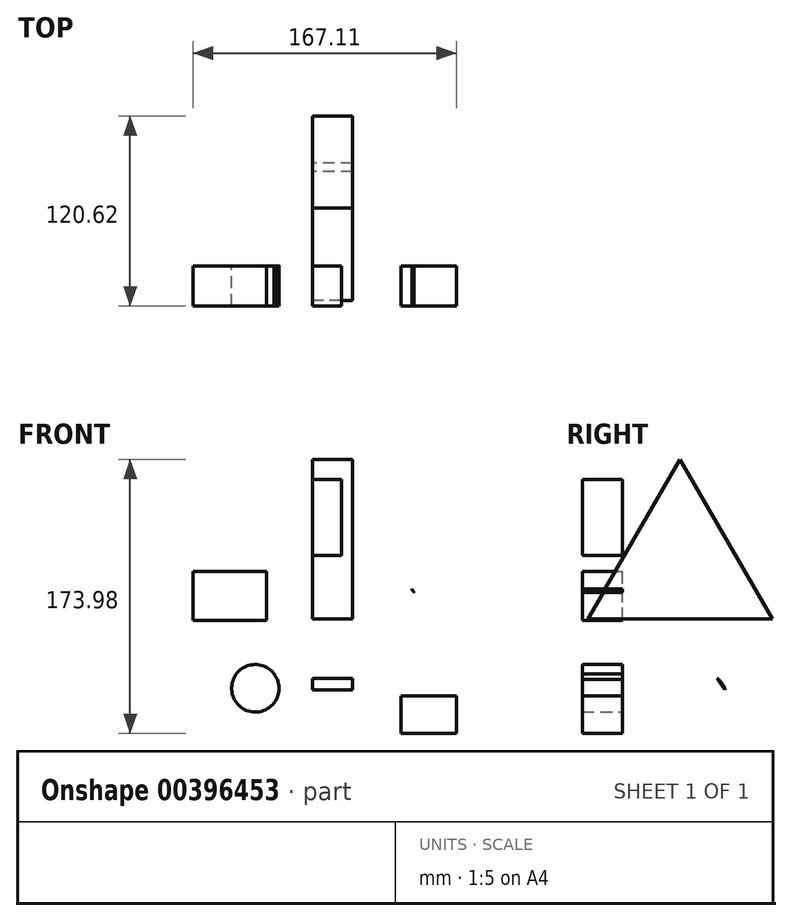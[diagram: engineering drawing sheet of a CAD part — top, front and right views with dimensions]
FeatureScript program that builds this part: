
annotation { "Feature Type Name" : "Feature", "Feature Type Description" : "" }
export const myFeature = defineFeature(function(context is Context, id is Id, definition is map)
    precondition{}
    {
        {
            var Q0;
            Q0=qCreatedBy(makeId("Front.planeOp"),FACE);
            var sketch = newSketch(context, id + "F0", { "sketchPlane" : qUnion([Q0])});
            skCircle(sketch, "E0", {"center": v(21.2, 12.78) * mm, "radius": 51.47 * mm});
            skPoint(sketch, "E0.first.point", {"position": v(62.94, 42.9) * mm});
            skPoint(sketch, "E0.second.point", {"position": v(-22.4, -14.6) * mm});
            skPoint(sketch, "E0.third.point", {"position": v(-28.66, 0) * mm});
            skCircle(sketch, "E1", {"center": v(70.23, 46.45) * mm, "radius": 8.11 * mm});
            skPoint(sketch, "E1.second.point", {"position": v(75.6, 52.52) * mm});
            skPoint(sketch, "E1.third.point", {"position": v(77.52, 42.9) * mm});
            skCircle(sketch, "E2", {"center": v(-36.43, -20.12) * mm, "radius": 15.08 * mm});
            skPoint(sketch, "E2.second.point", {"position": v(-48.03, -29.76) * mm});
            skPoint(sketch, "E2.third.point", {"position": v(-36.88, -5.04) * mm});
            skLineSegment(sketch, "E3.bottom", {"start": v(-29.25, 23.04) * mm, "end": v(-75.87, 23.04) * mm});
            skLineSegment(sketch, "E3.top", {"start": v(-29.25, 54.17) * mm, "end": v(-75.87, 54.17) * mm});
            skLineSegment(sketch, "E3.left", {"start": v(-29.25, 23.04) * mm, "end": v(-29.25, 54.17) * mm});
            skLineSegment(sketch, "E3.right", {"start": v(-75.87, 23.04) * mm, "end": v(-75.87, 54.17) * mm});
            skLineSegment(sketch, "E4.bottom", {"start": v(56.14, -25) * mm, "end": v(91.24, -25) * mm});
            skLineSegment(sketch, "E4.top", {"start": v(56.14, -48.76) * mm, "end": v(91.24, -48.76) * mm});
            skLineSegment(sketch, "E4.left", {"start": v(56.14, -25) * mm, "end": v(56.14, -48.76) * mm});
            skLineSegment(sketch, "E4.right", {"start": v(91.24, -25) * mm, "end": v(91.24, -48.76) * mm});
            skLineSegment(sketch, "E5.bottom", {"start": v(18.33, 64.17) * mm, "end": v(0, 64.17) * mm});
            skLineSegment(sketch, "E5.top", {"start": v(18.33, 112.4) * mm, "end": v(0, 112.4) * mm});
            skLineSegment(sketch, "E5.left", {"start": v(18.33, 64.17) * mm, "end": v(18.33, 112.4) * mm});
            skLineSegment(sketch, "E5.right", {"start": v(0, 64.17) * mm, "end": v(0, 112.4) * mm});
            skLineSegment(sketch, "E6", {"start": v(91.24, -48.76) * mm, "end": v(137.36, -96.51) * mm});
            skSolve(sketch);
        }
        {
            var Q0;
            {var subQ0=sQuery(id+"F0.wireOp",EDGE,"E1");var subQ1=sQuery(id+"F0.wireOp",EDGE,"E0");var subQ2=makeQuery(id+"F0.imprint","INTERSECT",VERTEX,{"disambiguationData":[OD(0.0)],"derivedFrom":[subQ1,subQ0]});Q0=makeQuery(id+"F0.imprint","IMPRINT",FACE,{"disambiguationData":[TD([[makeQuery(id+"F0.imprint","IMPRINT",EDGE,{"disambiguationData":[TD([[subQ2,-1.0]])],"derivedFrom":subQ1}),1.0]])]});}
            var Q1;
            {var subQ0=sQuery(id+"F0.wireOp",EDGE,"E1");var subQ1=sQuery(id+"F0.wireOp",EDGE,"E0");var subQ2=makeQuery(id+"F0.imprint","INTERSECT",VERTEX,{"disambiguationData":[OD(0.0)],"derivedFrom":[subQ1,subQ0]});Q1=makeQuery(id+"F0.imprint","IMPRINT",FACE,{"disambiguationData":[TD([[makeQuery(id+"F0.imprint","IMPRINT",EDGE,{"disambiguationData":[TD([[subQ2,1.0]])],"derivedFrom":subQ1}),-1.0]])]});}
            var Q2;
            {var subQ0=sQuery(id+"F0.wireOp",EDGE,"E2");var subQ1=sQuery(id+"F0.wireOp",EDGE,"E0");var subQ2=makeQuery(id+"F0.imprint","INTERSECT",VERTEX,{"disambiguationData":[OD(0.0)],"derivedFrom":[subQ1,subQ0]});Q2=makeQuery(id+"F0.imprint","IMPRINT",FACE,{"disambiguationData":[TD([[makeQuery(id+"F0.imprint","IMPRINT",EDGE,{"disambiguationData":[TD([[subQ2,-1.0]])],"derivedFrom":subQ1}),-1.0]])]});}
            var Q3;
            Q3=makeQuery(id+"F0.imprint","IMPRINT",FACE,{"disambiguationData":[TD([[makeQuery(id+"F0.imprint","IMPRINT",EDGE,{"derivedFrom":sQuery(id+"F0.wireOp",EDGE,"E5.bottom")}),-1.0]])]});
            var Q4;
            Q4=makeQuery(id+"F0.imprint","IMPRINT",FACE,{"disambiguationData":[TD([[makeQuery(id+"F0.imprint","IMPRINT",EDGE,{"derivedFrom":sQuery(id+"F0.wireOp",EDGE,"E3.bottom")}),-1.0]])]});
            var Q5;
            Q5=makeQuery(id+"F0.imprint","IMPRINT",FACE,{"disambiguationData":[TD([[makeQuery(id+"F0.imprint","IMPRINT",EDGE,{"derivedFrom":sQuery(id+"F0.wireOp",EDGE,"E4.bottom")}),-1.0]])]});
            extrude(context, id + "F1", {"entities" : qUnion([Q0, Q1, Q2, Q3, Q4, Q5]), "depth" : 25.4 * mm});
        }
        {
            var Q0;
            Q0=qCreatedBy(makeId("Right.planeOp"),FACE);
            var sketch = newSketch(context, id + "F2", { "sketchPlane" : qUnion([Q0])});
            skCircle(sketch, "E7", {"center": v(53.2, -24.21) * mm, "radius": 12.51 * mm});
            skPoint(sketch, "E7.first.point", {"position": v(64.58, -29.42) * mm});
            skPoint(sketch, "E7.second.point", {"position": v(49.89, -12.15) * mm});
            skPoint(sketch, "E7.third.point", {"position": v(65.66, -23) * mm});
            skCircle(sketch, "E8", {"center": v(103.74, 11.67) * mm, "radius": 50.5 * mm});
            skPoint(sketch, "E8.first.point", {"position": v(60.14, -13.8) * mm});
            skPoint(sketch, "E8.second.point", {"position": v(53.3, 9.31) * mm});
            skPoint(sketch, "E8.third.point", {"position": v(53.83, 4.01) * mm});
            skCircle(sketch, "E9", {"center": v(56.1, -42.6) * mm, "radius": 7.09 * mm});
            skPoint(sketch, "E9.first.point", {"position": v(58, -35.77) * mm});
            skPoint(sketch, "E9.second.point", {"position": v(63.17, -42.16) * mm});
            skPoint(sketch, "E9.third.point", {"position": v(61.25, -37.73) * mm});
            skSolve(sketch);
        }
        {
            var Q0;
            {var subQ0=sQuery(id+"F2.wireOp",EDGE,"E8");var subQ1=sQuery(id+"F2.wireOp",EDGE,"E7");var subQ2=makeQuery(id+"F2.imprint","INTERSECT",VERTEX,{"disambiguationData":[OD(0.0)],"derivedFrom":[subQ1,subQ0]});Q0=makeQuery(id+"F2.imprint","IMPRINT",FACE,{"disambiguationData":[TD([[makeQuery(id+"F2.imprint","IMPRINT",EDGE,{"disambiguationData":[TD([[subQ2,1.0]])],"derivedFrom":subQ1}),-1.0]])]});}
            var Q1;
            {var subQ0=sQuery(id+"F2.wireOp",EDGE,"E8");var subQ1=sQuery(id+"F2.wireOp",EDGE,"E7");var subQ2=makeQuery(id+"F2.imprint","INTERSECT",VERTEX,{"disambiguationData":[OD(0.0)],"derivedFrom":[subQ1,subQ0]});Q1=makeQuery(id+"F2.imprint","IMPRINT",FACE,{"disambiguationData":[TD([[makeQuery(id+"F2.imprint","IMPRINT",EDGE,{"disambiguationData":[TD([[subQ2,-1.0]])],"derivedFrom":subQ1}),1.0]])]});}
            var Q2;
            {var subQ0=sQuery(id+"F2.wireOp",EDGE,"E9");var subQ1=sQuery(id+"F2.wireOp",EDGE,"E7");var subQ2=makeQuery(id+"F2.imprint","INTERSECT",VERTEX,{"disambiguationData":[OD(0.0)],"derivedFrom":[subQ1,subQ0]});Q2=makeQuery(id+"F2.imprint","IMPRINT",FACE,{"disambiguationData":[TD([[makeQuery(id+"F2.imprint","IMPRINT",EDGE,{"disambiguationData":[TD([[subQ2,-1.0]])],"derivedFrom":subQ1}),-1.0]])]});}
            extrude(context, id + "F3", {"entities" : qUnion([Q0, Q1, Q2]), "depth" : 25.4 * mm});
        }
        {
            var Q0;
            Q0=qCreatedBy(makeId("Right.planeOp"),FACE);
            var sketch = newSketch(context, id + "F4", { "sketchPlane" : qUnion([Q0])});
            skCircle(sketch, "E10.cCircle", {"center": v(36.68, 57.62) * mm, "radius": 33.8 * mm, "construction": true});
            skLineSegment(sketch, "E10.0", {"start": v(95.22, 23.82) * mm, "end": v(-21.87, 23.82) * mm});
            skLineSegment(sketch, "E10.1", {"start": v(-21.87, 23.82) * mm, "end": v(36.68, 125.22) * mm});
            skLineSegment(sketch, "E10.2", {"start": v(36.68, 125.22) * mm, "end": v(95.22, 23.82) * mm});
            skPoint(sketch, "E10.0.midPoint", {"position": v(36.68, 23.82) * mm});
            skSolve(sketch);
        }
        {
            var Q0;
            Q0=makeQuery(id+"F4.imprint","IMPRINT",FACE,{"disambiguationData":[TD([[makeQuery(id+"F4.imprint","IMPRINT",EDGE,{"derivedFrom":sQuery(id+"F4.wireOp",EDGE,"E10.0")}),-1.0]])]});
            extrude(context, id + "F5", {"entities" : qUnion([Q0]), "depth" : 25.4 * mm});
        }
    });
